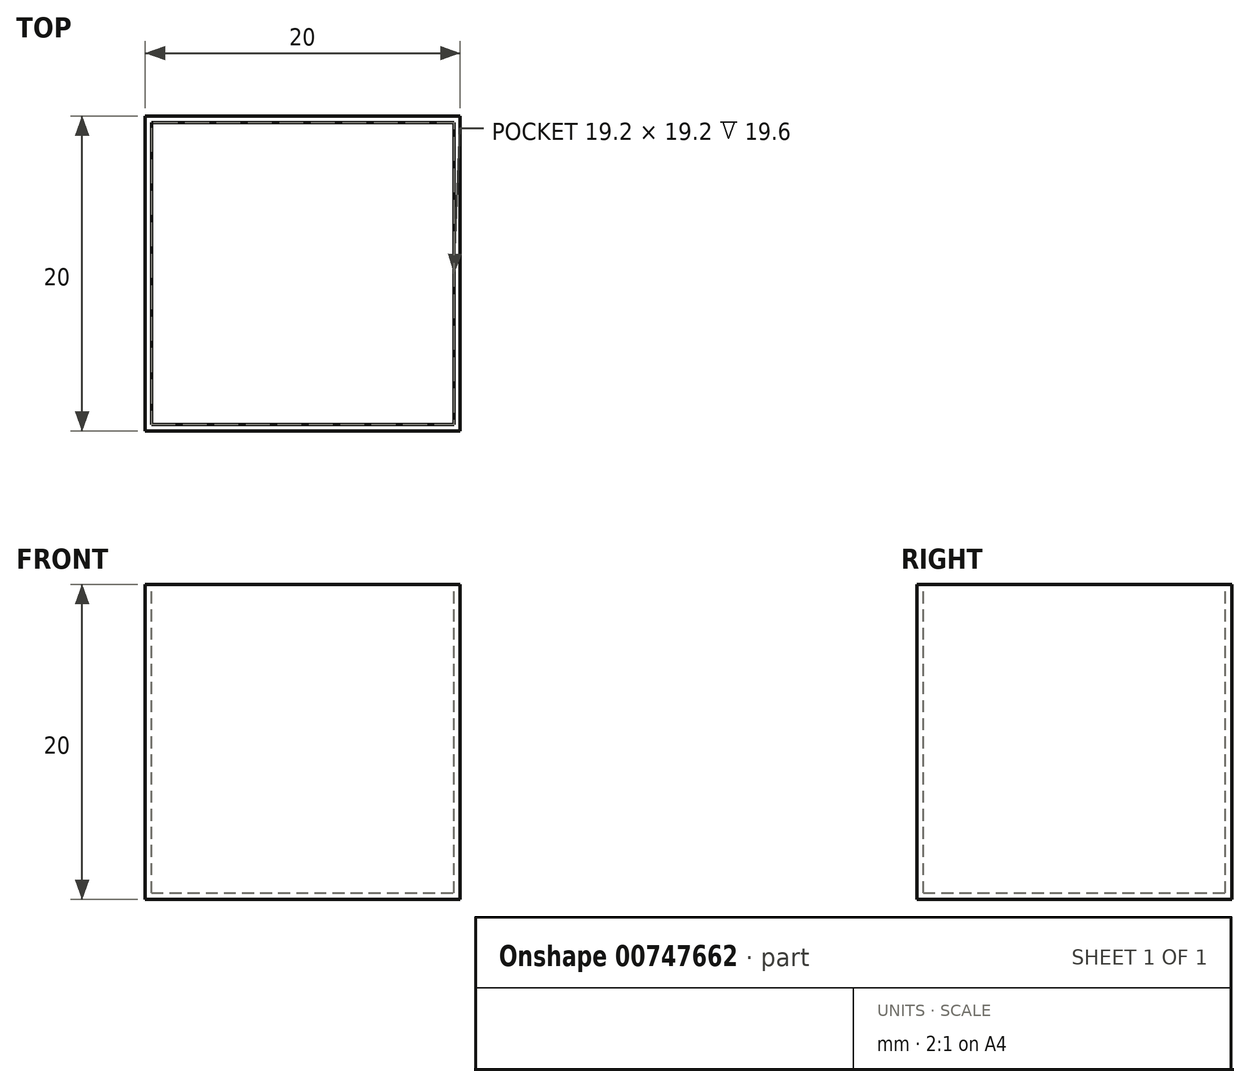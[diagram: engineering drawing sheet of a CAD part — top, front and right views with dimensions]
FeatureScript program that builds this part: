
annotation { "Feature Type Name" : "Feature", "Feature Type Description" : "" }
export const myFeature = defineFeature(function(context is Context, id is Id, definition is map)
    precondition{}
    {
        {
            var Q0;
            Q0=qCreatedBy(makeId("Front.planeOp"),FACE);
            var sketch = newSketch(context, id + "F0", { "sketchPlane" : qUnion([Q0])});
            skLineSegment(sketch, "E0.bottom", {"start": v(0, 0) * mm, "end": v(20, 0) * mm});
            skLineSegment(sketch, "E0.top", {"start": v(0, 20) * mm, "end": v(20, 20) * mm});
            skLineSegment(sketch, "E0.left", {"start": v(0, 0) * mm, "end": v(0, 20) * mm});
            skLineSegment(sketch, "E0.right", {"start": v(20, 0) * mm, "end": v(20, 20) * mm});
            skSolve(sketch);
        }
        {
            var Q0;
            Q0=makeQuery(id+"F0.imprint","IMPRINT",FACE,{"disambiguationData":[TD([[makeQuery(id+"F0.imprint","IMPRINT",EDGE,{"derivedFrom":sQuery(id+"F0.wireOp",EDGE,"E0.bottom")}),1.0]])]});
            extrude(context, id + "F1", {"entities" : qUnion([Q0]), "depth" : 20 * mm, "offsetDistance" : 25 * mm});
        }
        {
            var Q0;
            Q0=makeQuery(id+"F1.opExtrude","SWEPT_FACE",FACE,{"disambiguationData":[OSD([sQuery(id+"F0.wireOp",EDGE,"E0.top")])]});
            shell(context, id + "F2", {"entities" : qUnion([Q0]), "thickness" : .4 * mm});
        }
    });
